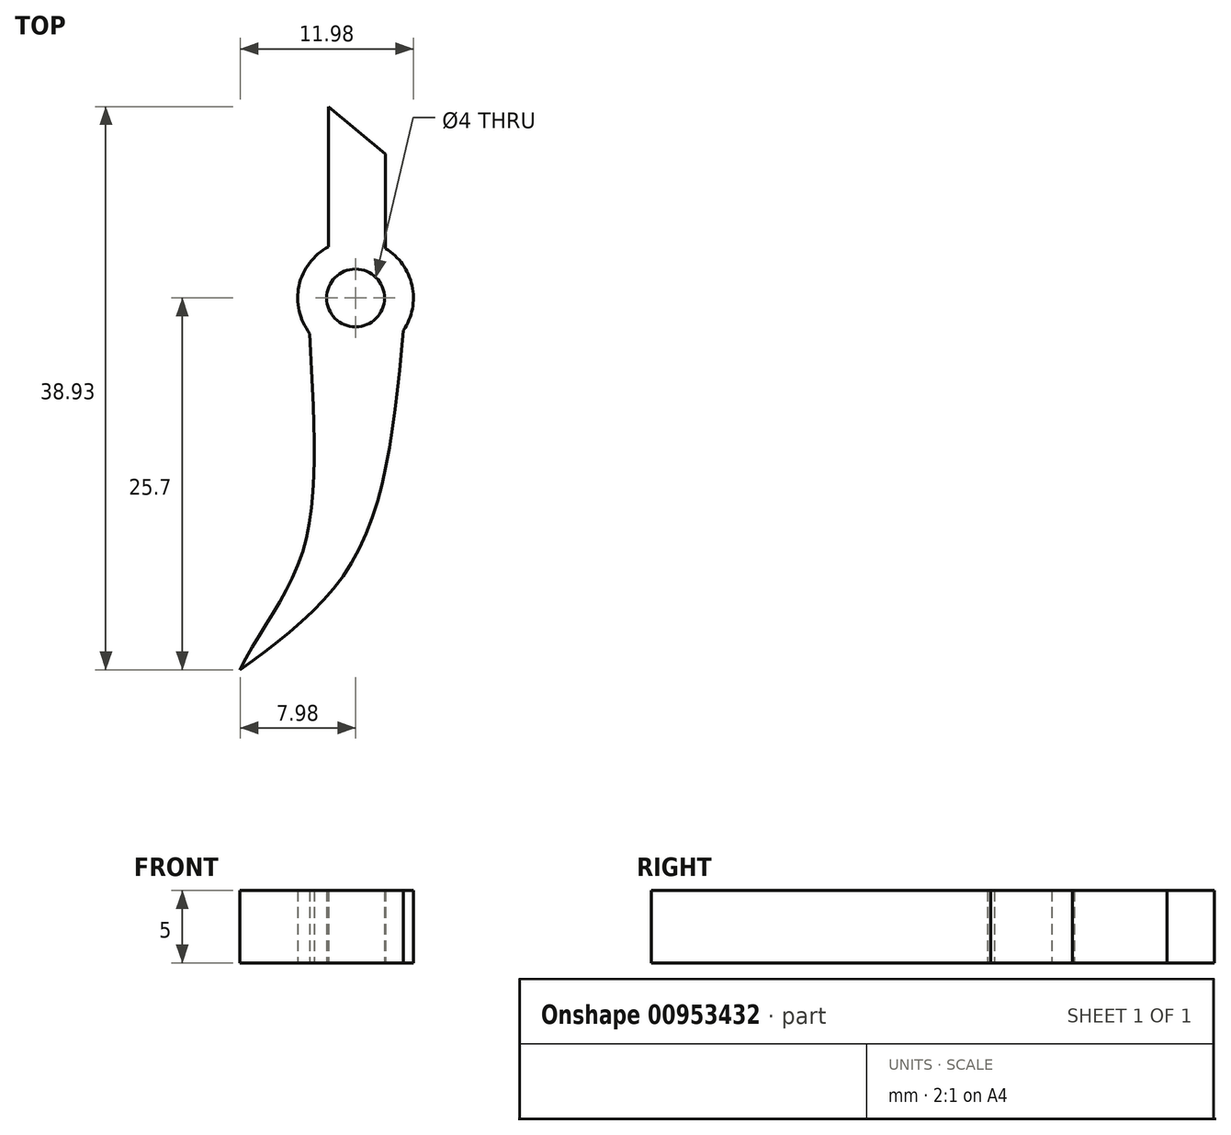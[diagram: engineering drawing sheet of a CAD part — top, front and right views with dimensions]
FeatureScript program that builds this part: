
annotation { "Feature Type Name" : "Feature", "Feature Type Description" : "" }
export const myFeature = defineFeature(function(context is Context, id is Id, definition is map)
    precondition{}
    {
        {
            var Q0;
            Q0=qCreatedBy(makeId("Top.planeOp"),FACE);
            var sketch = newSketch(context, id + "F0", { "sketchPlane" : qUnion([Q0])});
            skCircle(sketch, "E0", {"center": v(0, 0) * mm, "radius": 4 * mm});
            skFitSpline(sketch, "E1", {"points": [v(-3.16, -2.45) * mm, v(-3.6, -17.4) * mm, v(-7.98, -25.7) * mm], "startDerivative": vector(1, -28.74) * mm, "endDerivative": vector(-8.85, -18.7) * mm});
            skFitSpline(sketch, "E2", {"points": [v(3.31, -2.24) * mm, v(0, -17.83) * mm, v(-7.98, -25.7) * mm], "startDerivative": vector(-3, -31.76) * mm, "endDerivative": vector(-20.1, -14.66) * mm});
            skCircle(sketch, "E3", {"center": v(0, 0) * mm, "radius": 2 * mm});
            skLineSegment(sketch, "E4", {"start": v(-1.86, 3.54) * mm, "end": v(-1.86, 13.23) * mm});
            skLineSegment(sketch, "E5", {"start": v(-1.86, 13.23) * mm, "end": v(2.08, 9.95) * mm});
            skLineSegment(sketch, "E6", {"start": v(2.08, 9.95) * mm, "end": v(2.08, 3.42) * mm});
            skSolve(sketch);
        }
        {
            var Q0;
            {var subQ0=sQuery(id+"F0.wireOp",EDGE,"E4");Q0=makeQuery(id+"F0.imprint","IMPRINT",FACE,{"disambiguationData":[TD([[makeQuery(id+"F0.imprint","IMPRINT",EDGE,{"derivedFrom":subQ0}),-1.0]])]});}
            var Q1;
            Q1=makeQuery(id+"F0.imprint","IMPRINT",FACE,{"disambiguationData":[TD([[makeQuery(id+"F0.imprint","IMPRINT",EDGE,{"derivedFrom":sQuery(id+"F0.wireOp",EDGE,"E3")}),-1.0]])]});
            var Q2;
            {var subQ0=sQuery(id+"F0.wireOp",EDGE,"E1");Q2=makeQuery(id+"F0.imprint","IMPRINT",FACE,{"disambiguationData":[TD([[makeQuery(id+"F0.imprint","IMPRINT",EDGE,{"derivedFrom":subQ0}),1.0]])]});}
            extrude(context, id + "F1", {"entities" : qUnion([Q0, Q1, Q2]), "depth" : 5 * mm, "offsetDistance" : 25 * mm});
        }
    });
